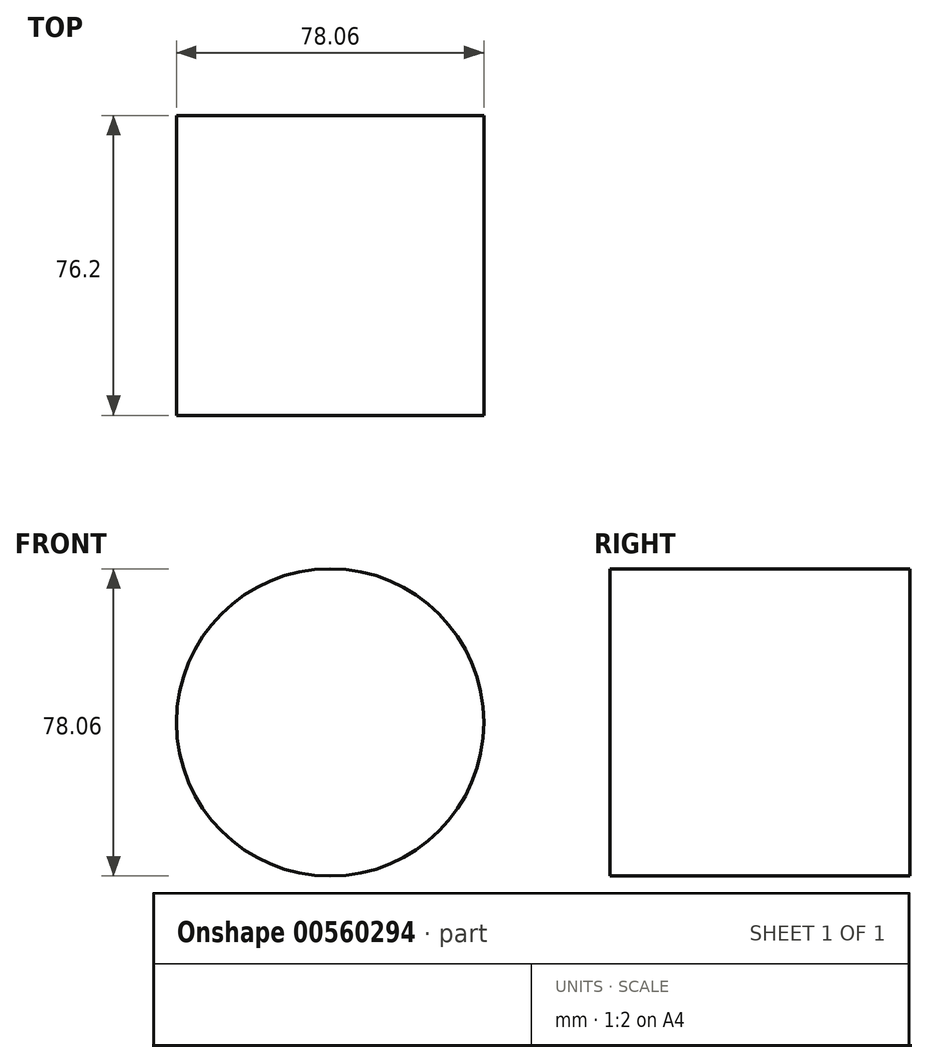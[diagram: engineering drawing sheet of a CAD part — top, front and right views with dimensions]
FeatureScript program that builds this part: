
annotation { "Feature Type Name" : "Feature", "Feature Type Description" : "" }
export const myFeature = defineFeature(function(context is Context, id is Id, definition is map)
    precondition{}
    {
        {
            var Q0;
            Q0=qCreatedBy(makeId("Front.planeOp"),FACE);
            var sketch = newSketch(context, id + "F0", { "sketchPlane" : qUnion([Q0])});
            skCircle(sketch, "E0", {"center": v(0, 0) * mm, "radius": 39.03 * mm});
            skSolve(sketch);
        }
        {
            var Q0;
            Q0=sQuery(id+"F0.wireOp",EDGE,"E0");
            extrude(context, id + "F1", {"bodyType" : ToolBodyType.SURFACE, "surfaceEntities" : qUnion([Q0]), "depth" : 50.8 * mm, "offsetDistance" : 25.4 * mm, "hasSecondDirection" : true, "secondDirectionOppositeDirection" : true, "secondDirectionDepth" : 25.4 * mm});
        }
    });
